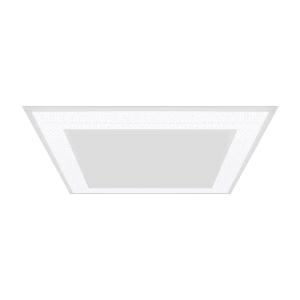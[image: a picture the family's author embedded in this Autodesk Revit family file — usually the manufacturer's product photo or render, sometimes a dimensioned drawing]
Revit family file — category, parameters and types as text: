
# Revit family: 3f_filippi_-_3f_eldorado_frame_white_lgs_3f_filippi_-_2327_-_3f_eldorado_39-840_dali_lgs_596
name_source: partatom
category: Lighting Fixtures
units: mm (PartAtom-declared; Revit-internal decimal feet)

## family parameters
Cut with Voids When Loaded = No
Host = Face
Light Source = No
Part Type = Normal
Room Calculation Point = No
Round Connector Dimension = Use Diameter
Shared = No

## types (1)
- 3F Filippi - 3F Eldorado Frame White LGS (1 x LED, 4256 lm, 45 W, 4000 K)
    Apparent Load = 45 VA
    Approval mark = ENEC
    CIE Flux Codes = 61 86 96 100 100
    Color Rendering = 80
    Color Temperature = 4000 K
    Control Gear = Electronic transformer
    Default Elevation = 1800 mm
    Description = ILLUMINOTECHNICAL
Luminous efficiency 100% (DLOR 100%, ULOR 0%).
Initial luminous flux of the luminaire 4256 lm.
Controlled symmetric distribution.
Installation Interdistance Transv.D = 1.08 x hu - Long.D = 1.08 x hu.
Average luminance <3000 cd/m² for radial angles >65°.
Tabular UGR (CIE 117 - 4H-8H; S=0.25H; 70/50/20): RUG 19.1 - 19.2.
Beam angle: 81° - 80°.
Luminous efficacy 95 lm/W.
Lifetime (L93/B10): 30000 h. (tq+25°C)
Lifetime (L90/B10): 50000 h. (tq+25°C)
Lifetime (L85/B10): 80000 h. (tq+25°C)
Lifetime (L80/B10): 100000 h. (tq+25°C)
Sudden decreased luminous flux after 50000 hours: 0% (C0).
Photobiological safety in compliance with IEC/TR 62778: RG0 risk exempt, (IEC 62471).
In compliance with IEC/EN 62722-2-1 - IEC/EN 62717 standards.

SOURCE
4 linear LED modules 9.75W/840.
Energy efficiency class (UE 2019/2020 - UE 2019/2015): D.
CIE 13.3 Colour rendering index: CRI >80 (R9 <50%).
IES TM-30 Fidelity Index: Rf = 84 Rg = 95.
CCT nominal colour temperature 4000 K.
Colour initial tolerance (MacAdam): SDCM 3.

MECHANICAL
Housing in hot-galvanised steel, painted in white polyester.
LGS micro-prismatic flat diffuser in transparent methacrylate (PMMA), multi-lenticular exterior, anti-glare.
Anti-glare opal polycarbonate filter for brightness uniformity.
Central part in hot-galvanised steel, painted in white polyester.
Luminaire with limited surface temperature. - D - (EN 60598-2-24)
Dimensions: 596x596 mm, height 65 mm. Weight 5.5 kg.
IP40 protection degree.
Mechanical strength to impacts IK02 (0.2 joule).
Glow-wire test resistance 650°C.

ELECTRICAL
Halogen Free DALI-2, PUSH-DIM, electronic wiring 230V-50/60Hz, power factor 0.95 at full load, THD <25%, constant output current, SELV, class I, 1 driver, 1 DALI addresse.
Power of the luminaire 45 W.
CE - IEC 60598-1 - EN 60598-1.
SAFE FLICKER: PstLM=<1 and SVM=<0.4 (IEC TR 61547-1 and IEC TR 63158), to ensure a more comfortable and safe light.
Luminaire compliant with EN 60598-2-22 for power supply from a centralised emergency system CPSS (Central Power Supply System), not incorporated in the luminaire - high risk areas excluded. The default power and flux are 100% in AC and 15% in DC.
Ambient temperature from 0°C to +25°C.
Temperature class T6 max 85°C.
Relative humidity UR: <85%.

INSTALLATION
Lay-in recessed fitting.
All accessories dedicated to this product are available on the Catalog and on our website www.3F-Filippi.com.

APPLICATIONS
Any environment in which flexibility of lighting and customisation is required, capable of integrating perfectly into the areas and furnishings of different workspaces.
Environments: with VDTs, meeting rooms, offices.
Environments: architectural, commercial, staterooms, banks.
Environments where dynamic, soft and diffuse light is required for optimal visual comfort.

LIGHT MANAGEMENT
Recommended minimum setting: 10%.
The device, equipped with DALI-2 driver, can be controlled manually with 3F Easy Dim technology or automatically/manually with 3F Smart Dimming technology and/or centralised DALI systems.
DALI-2 certification guarantees interoperability with other devices with the same certification.
In electrical systems without a regulation system (manual or automatic) and DALI bus, a suitable jumper must be made on the DA-DA terminals of the appliance.

WARNING
Luminaire designed for disposal/recycling at end-of-life.
Replaceable (LED only) light source by a professional. Replaceable control gear by a professional.
    Height = 0 mm  [stored 0 ft]
    Lamp = 1 x LED
    Lamp Light Flux = 4256 lm
    Lamp Power = 45 W
    Lamp count = 1
    Length = 596 mm
    Lifetime = 50000 h
    Luminous efficacy = 95 lm/W
    Manufacturer = 3F Filippi
    ModVariant = No
    Model = 3F Filippi - 2327 - 3F Eldorado 39-840 DALI LGS 596
    Mounting Place = Ceiling
    Mounting Type = Recessed
    Number of Poles = 1
    OnlyDefault = Yes
    Power Factor = 1
    Product Name = 3F Filippi - 3F Eldorado Frame White LGS
    Product group = recessed luminaire
    ProductGroupID = 4
    Protection Class = Protection class I
    Protection Degree = IP 40
    RLX_Detail_Level = 1
    RLX_Emergency_Light_Flux = 0 lm
    RLX_Emergency_Type = 0
    RLX_Emergency_Type_DB = No
    RlxData = <blob elided: 125481 chars, md5=02e6f7ba>
    Socket = socket
    Standby Power = 0 W
    System Light Flux = 4256 lm
    System Power = 45 W
    Type Comments = Product without accessories
    Type Image = 3ffilippi_3f_eldorado_frame_white_lgs.jpg
    URL = http://relux.com
    VarID = ---
    Voltage = 0 V
    Weight = 0.00 kg
    Width = 596 mm

note: [stored X ft] marks values corroborated as IEEE doubles in the binary element streams (Revit-internal decimal feet)

## geometry (parser evidence)
native form markers: Blend x4, Sweep x12
no freeform markers — native parametric forms only
